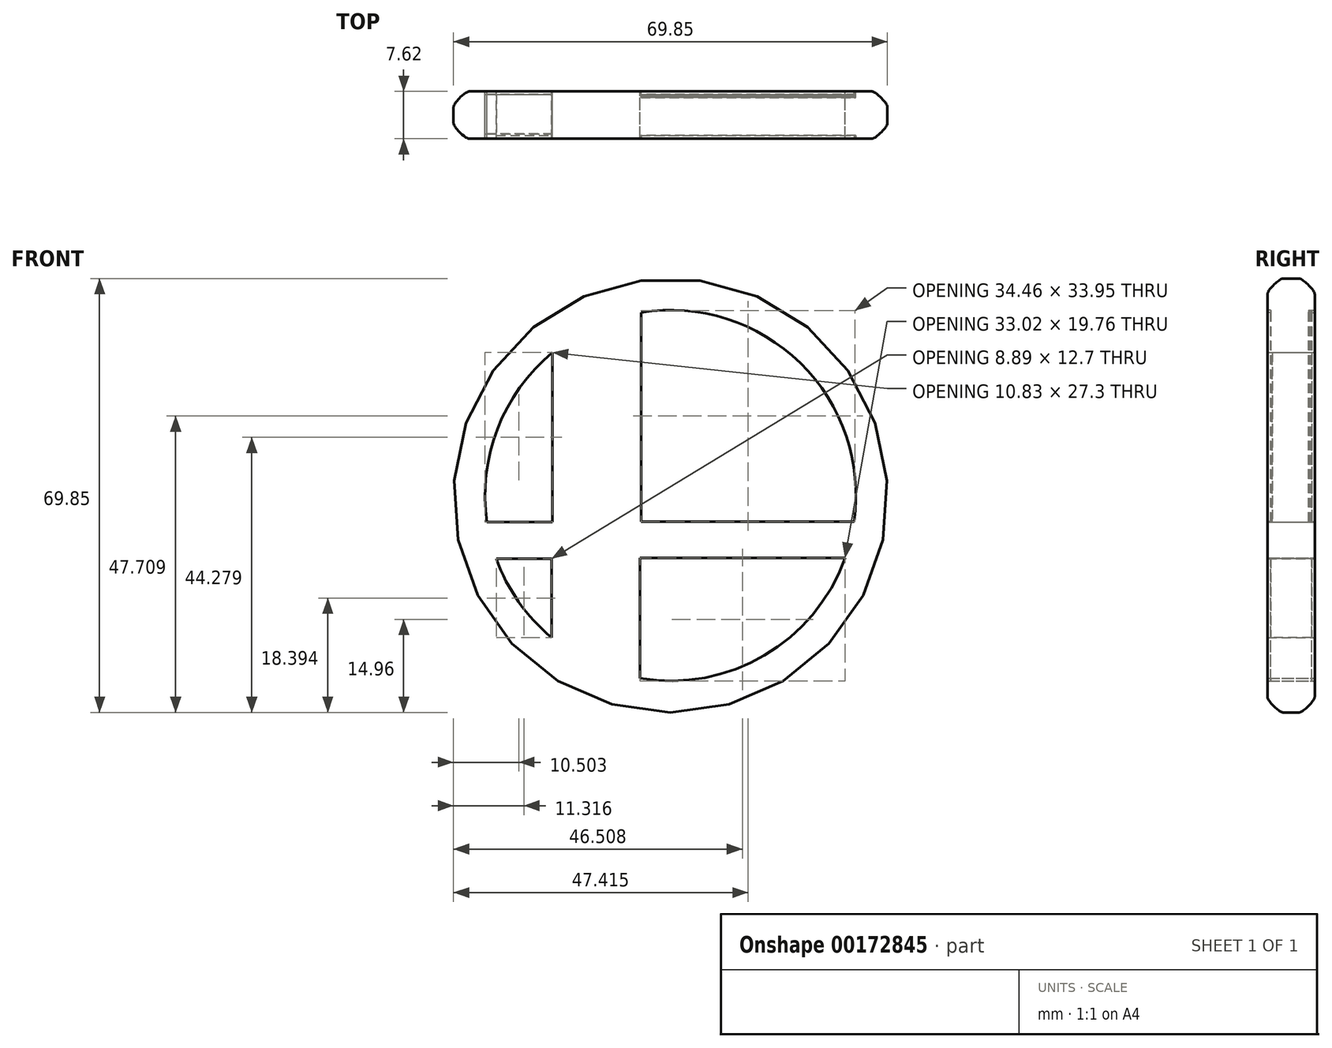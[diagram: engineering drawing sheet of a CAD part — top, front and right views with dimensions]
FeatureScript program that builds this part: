
annotation { "Feature Type Name" : "Feature", "Feature Type Description" : "" }
export const myFeature = defineFeature(function(context is Context, id is Id, definition is map)
    precondition{}
    {
        {
            var Q0;
            Q0=qCreatedBy(makeId("Front.planeOp"),FACE);
            var sketch = newSketch(context, id + "F0", { "sketchPlane" : qUnion([Q0])});
            skLineSegment(sketch, "E0", {"start": v(0, 0) * mm, "end": v(31.75, 0) * mm});
            skCircle(sketch, "E1", {"center": v(31.4, 32.14) * mm, "radius": 34.93 * mm});
            skCircle(sketch, "E2", {"center": v(31.4, 32.14) * mm, "radius": 29.85 * mm});
            skLineSegment(sketch, "E3", {"start": v(1.87, 27.85) * mm, "end": v(12.4, 27.85) * mm});
            skLineSegment(sketch, "E4", {"start": v(12.4, 27.85) * mm, "end": v(12.4, 55.15) * mm});
            skLineSegment(sketch, "E5", {"start": v(26.67, 61.6) * mm, "end": v(26.67, 27.95) * mm});
            skLineSegment(sketch, "E6", {"start": v(26.67, 27.95) * mm, "end": v(60.96, 27.95) * mm});
            skLineSegment(sketch, "E7", {"start": v(3.35, 21.96) * mm, "end": v(12.24, 21.96) * mm});
            skLineSegment(sketch, "E8", {"start": v(12.24, 21.96) * mm, "end": v(12.24, 9.26) * mm});
            skLineSegment(sketch, "E9", {"start": v(26.48, 2.7) * mm, "end": v(26.48, 22.06) * mm});
            skLineSegment(sketch, "E10", {"start": v(26.48, 22.06) * mm, "end": v(59.5, 22.06) * mm});
            skSolve(sketch);
        }
        {
            var Q0;
            Q0=makeQuery(id+"F0.imprint","IMPRINT",FACE,{"disambiguationData":[TD([[makeQuery(id+"F0.imprint","IMPRINT",EDGE,{"derivedFrom":sQuery(id+"F0.wireOp",EDGE,"E1")}),1.0]])]});
            var Q1;
            {var subQ2=sQuery(id+"F0.wireOp",EDGE,"E3");Q1=makeQuery(id+"F0.imprint","IMPRINT",FACE,{"disambiguationData":[TD([[makeQuery(id+"F0.imprint","IMPRINT",EDGE,{"derivedFrom":subQ2}),-1.0]])]});}
            extrude(context, id + "F1", {"entities" : qUnion([Q0, Q1]), "depth" : 7.62 * mm});
        }
        {
            var Q0;
            Q0=makeQuery(id+"F1.opExtrude","CAP_EDGE",EDGE,{"disambiguationData":[OSD([sQuery(id+"F0.wireOp",EDGE,"E1")])],"isStart":false});
            fillet(context, id + "F2", {"entities" : qUnion([Q0]), "radius" : 2.54 * mm, "tangentPropagation" : true, "rho" : 0.2, "crossSection" : FilletCrossSection.CONIC, "allowEdgeOverflow" : false});
        }
        {
            var Q0;
            Q0=makeQuery(id+"F1.opExtrude","CAP_FACE",FACE,{"disambiguationData":[OSD([sQuery(id+"F0.wireOp",EDGE,"E1"),sQuery(id+"F0.wireOp",EDGE,"E2"),sQuery(id+"F0.wireOp",EDGE,"E3"),sQuery(id+"F0.wireOp",EDGE,"E4"),sQuery(id+"F0.wireOp",EDGE,"E5"),sQuery(id+"F0.wireOp",EDGE,"E6"),sQuery(id+"F0.wireOp",EDGE,"E7"),sQuery(id+"F0.wireOp",EDGE,"E8"),sQuery(id+"F0.wireOp",EDGE,"E9"),sQuery(id+"F0.wireOp",EDGE,"E10")])],"isStart":false});
            var sketch = newSketch(context, id + "F3", { "sketchPlane" : qUnion([Q0])});
            skLineSegment(sketch, "E11", {"start": v(26.67, 61.6) * mm, "end": v(26.67, 27.95) * mm});
            skLineSegment(sketch, "E12", {"start": v(26.67, 27.95) * mm, "end": v(60.96, 27.95) * mm});
            skSolve(sketch);
        }
        {
            var Q0;
            Q0=makeQuery(id+"F3.imprint","IMPRINT",FACE,{"disambiguationData":[TD([[makeQuery(id+"F3.imprint","IMPRINT",EDGE,{"derivedFrom":sQuery(id+"F3.wireOp",EDGE,"E11")}),1.0]])]});
            var Q1;
            Q1 = qSketchRegion(id + "F7r4KU7YKBrCE7T_1", true);
            extrude(context, id + "F4", {"entities" : qUnion([Q0, Q1]), "depth" : 25.4 * mm});
        }
        {
            var Q0;
            Q0=makeQuery(id+"F4.opExtrude","CAP_FACE",FACE,{"disambiguationData":[OSD([sQuery(id+"F0.wireOp",EDGE,"E2"),sQuery(id+"F3.wireOp",EDGE,"E11"),sQuery(id+"F3.wireOp",EDGE,"E12")])],"isStart":true});
            extrude(context, id + "F5", {"entities" : qUnion([Q0]), "depth" : 7.11 * mm, "hasSecondDirection" : true, "secondDirectionOppositeDirection" : true, "secondDirectionDepth" : 20.32 * mm});
        }
        {
            var Q0;
            Q0=makeQuery(id+"F5.opExtrude","CAP_FACE",FACE,{"disambiguationData":[OSD([sQuery(id+"F0.wireOp",EDGE,"E2"),sQuery(id+"F3.wireOp",EDGE,"E11"),sQuery(id+"F3.wireOp",EDGE,"E12")])],"isStart":false});
            extrude(context, id + "F6", {"entities" : qUnion([Q0]), "operationType" : NewBodyOperationType.ADD, "oppositeDirection" : true, "depth" : 1.02 * mm});
        }
        {
            var Q0;
            Q0=makeQuery(id+"F4.opExtrude","CAP_FACE",FACE,{"disambiguationData":[OSD([sQuery(id+"F0.wireOp",EDGE,"E2"),sQuery(id+"F3.wireOp",EDGE,"E11"),sQuery(id+"F3.wireOp",EDGE,"E12")])],"isStart":false});
            extrude(context, id + "F7", {"entities" : qUnion([Q0]), "oppositeDirection" : true, "depth" : 25.4 * mm});
        }
        {
            var Q0;
            Q0=makeQuery(id+"F4.opExtrude","CAP_FACE",FACE,{"disambiguationData":[OSD([sQuery(id+"F0.wireOp",EDGE,"E2"),sQuery(id+"F3.wireOp",EDGE,"E11"),sQuery(id+"F3.wireOp",EDGE,"E12")])],"isStart":false});
            extrude(context, id + "F8", {"entities" : qUnion([Q0]), "oppositeDirection" : true, "depth" : 25.4 * mm});
        }
        {
            var Q0;
            Q0=makeQuery(id+"F4.opExtrude","CAP_FACE",FACE,{"disambiguationData":[OSD([sQuery(id+"F0.wireOp",EDGE,"E2"),sQuery(id+"F3.wireOp",EDGE,"E11"),sQuery(id+"F3.wireOp",EDGE,"E12")])],"isStart":false});
            extrude(context, id + "F9", {"entities" : qUnion([Q0]), "operationType" : NewBodyOperationType.REMOVE, "oppositeDirection" : true, "depth" : 25.9 * mm});
        }
        {
            var Q0;
            Q0=makeQuery(id+"F5.opExtrude","CAP_FACE",FACE,{"disambiguationData":[OSD([sQuery(id+"F0.wireOp",EDGE,"E2"),sQuery(id+"F3.wireOp",EDGE,"E11"),sQuery(id+"F3.wireOp",EDGE,"E12")])],"isStart":false});
            extrude(context, id + "F10", {"entities" : qUnion([Q0]), "oppositeDirection" : true, "depth" : 0.5 * mm});
        }
        {
            var Q0;
            Q0=makeQuery(id+"F5.opExtrude","CAP_FACE",FACE,{"disambiguationData":[OSD([sQuery(id+"F0.wireOp",EDGE,"E2"),sQuery(id+"F3.wireOp",EDGE,"E11"),sQuery(id+"F3.wireOp",EDGE,"E12")])],"isStart":false});
            extrude(context, id + "F11", {"entities" : qUnion([Q0]), "oppositeDirection" : true, "depth" : 0.25 * mm});
        }
        {
            var Q0;
            Q0=makeQuery(id+"F1.opExtrude","CAP_FACE",FACE,{"disambiguationData":[OSD([sQuery(id+"F0.wireOp",EDGE,"E1"),sQuery(id+"F0.wireOp",EDGE,"E2"),sQuery(id+"F0.wireOp",EDGE,"E3"),sQuery(id+"F0.wireOp",EDGE,"E4"),sQuery(id+"F0.wireOp",EDGE,"E5"),sQuery(id+"F0.wireOp",EDGE,"E6"),sQuery(id+"F0.wireOp",EDGE,"E7"),sQuery(id+"F0.wireOp",EDGE,"E8"),sQuery(id+"F0.wireOp",EDGE,"E9"),sQuery(id+"F0.wireOp",EDGE,"E10")])],"isStart":true});
            var sketch = newSketch(context, id + "F12", { "sketchPlane" : qUnion([Q0])});
            skLineSegment(sketch, "E13", {"start": v(-59.5, 22.06) * mm, "end": v(-26.48, 22.06) * mm});
            skLineSegment(sketch, "E14", {"start": v(-26.48, 22.06) * mm, "end": v(-26.48, 2.7) * mm});
            skSolve(sketch);
        }
        {
            var Q0;
            Q0=makeQuery(id+"F12.imprint","IMPRINT",FACE,{"disambiguationData":[TD([[makeQuery(id+"F12.imprint","IMPRINT",EDGE,{"derivedFrom":sQuery(id+"F12.wireOp",EDGE,"E13")}),1.0]])]});
            extrude(context, id + "F13", {"entities" : qUnion([Q0]), "oppositeDirection" : true, "depth" : 7.11 * mm, "hasSecondDirection" : true, "secondDirectionOppositeDirection" : true, "secondDirectionDepth" : 0.5 * mm});
        }
        {
            var Q0;
            Q0=makeQuery(id+"F1.opExtrude","CAP_FACE",FACE,{"disambiguationData":[OSD([sQuery(id+"F0.wireOp",EDGE,"E1"),sQuery(id+"F0.wireOp",EDGE,"E2"),sQuery(id+"F0.wireOp",EDGE,"E3"),sQuery(id+"F0.wireOp",EDGE,"E4"),sQuery(id+"F0.wireOp",EDGE,"E5"),sQuery(id+"F0.wireOp",EDGE,"E6"),sQuery(id+"F0.wireOp",EDGE,"E7"),sQuery(id+"F0.wireOp",EDGE,"E8"),sQuery(id+"F0.wireOp",EDGE,"E9"),sQuery(id+"F0.wireOp",EDGE,"E10")])],"isStart":true});
            var sketch = newSketch(context, id + "F14", { "sketchPlane" : qUnion([Q0])});
            skLineSegment(sketch, "E15", {"start": v(-12.4, 27.85) * mm, "end": v(-1.87, 27.85) * mm});
            skLineSegment(sketch, "E16", {"start": v(-12.4, 55.15) * mm, "end": v(-12.4, 27.85) * mm});
            skSolve(sketch);
        }
        {
            var Q0;
            Q0=makeQuery(id+"F14.imprint","IMPRINT",FACE,{"disambiguationData":[TD([[makeQuery(id+"F14.imprint","IMPRINT",EDGE,{"derivedFrom":sQuery(id+"F14.wireOp",EDGE,"E15")}),-1.0]])]});
            extrude(context, id + "F15", {"entities" : qUnion([Q0]), "oppositeDirection" : true, "depth" : 6.86 * mm, "hasSecondDirection" : true, "secondDirectionOppositeDirection" : true, "secondDirectionDepth" : 0.5 * mm});
        }
        {
            var Q0;
            Q0=makeQuery(id+"F1.opExtrude","CAP_FACE",FACE,{"disambiguationData":[OSD([sQuery(id+"F0.wireOp",EDGE,"E1"),sQuery(id+"F0.wireOp",EDGE,"E2"),sQuery(id+"F0.wireOp",EDGE,"E3"),sQuery(id+"F0.wireOp",EDGE,"E4"),sQuery(id+"F0.wireOp",EDGE,"E5"),sQuery(id+"F0.wireOp",EDGE,"E6"),sQuery(id+"F0.wireOp",EDGE,"E7"),sQuery(id+"F0.wireOp",EDGE,"E8"),sQuery(id+"F0.wireOp",EDGE,"E9"),sQuery(id+"F0.wireOp",EDGE,"E10")])],"isStart":false});
            var sketch = newSketch(context, id + "F16", { "sketchPlane" : qUnion([Q0])});
            skLineSegment(sketch, "E17", {"start": v(3.35, 21.96) * mm, "end": v(12.24, 21.96) * mm});
            skLineSegment(sketch, "E18", {"start": v(12.24, 21.96) * mm, "end": v(12.24, 9.26) * mm});
            skSolve(sketch);
        }
        {
            var Q0;
            Q0=makeQuery(id+"F16.imprint","IMPRINT",FACE,{"disambiguationData":[TD([[makeQuery(id+"F16.imprint","IMPRINT",EDGE,{"derivedFrom":sQuery(id+"F16.wireOp",EDGE,"E17")}),-1.0]])]});
            extrude(context, id + "F17", {"entities" : qUnion([Q0]), "oppositeDirection" : true, "depth" : 7.11 * mm, "hasSecondDirection" : true, "secondDirectionOppositeDirection" : true, "secondDirectionDepth" : 0.5 * mm});
        }
        {
            var Q0;
            Q0=makeQuery(id+"F1.opExtrude","CAP_EDGE",EDGE,{"disambiguationData":[OSD([sQuery(id+"F0.wireOp",EDGE,"E1")])],"isStart":true});
            fillet(context, id + "F18", {"entities" : qUnion([Q0]), "radius" : 2.54 * mm, "rho" : .2, "crossSection" : FilletCrossSection.CONIC, "allowEdgeOverflow" : false});
        }
    });
